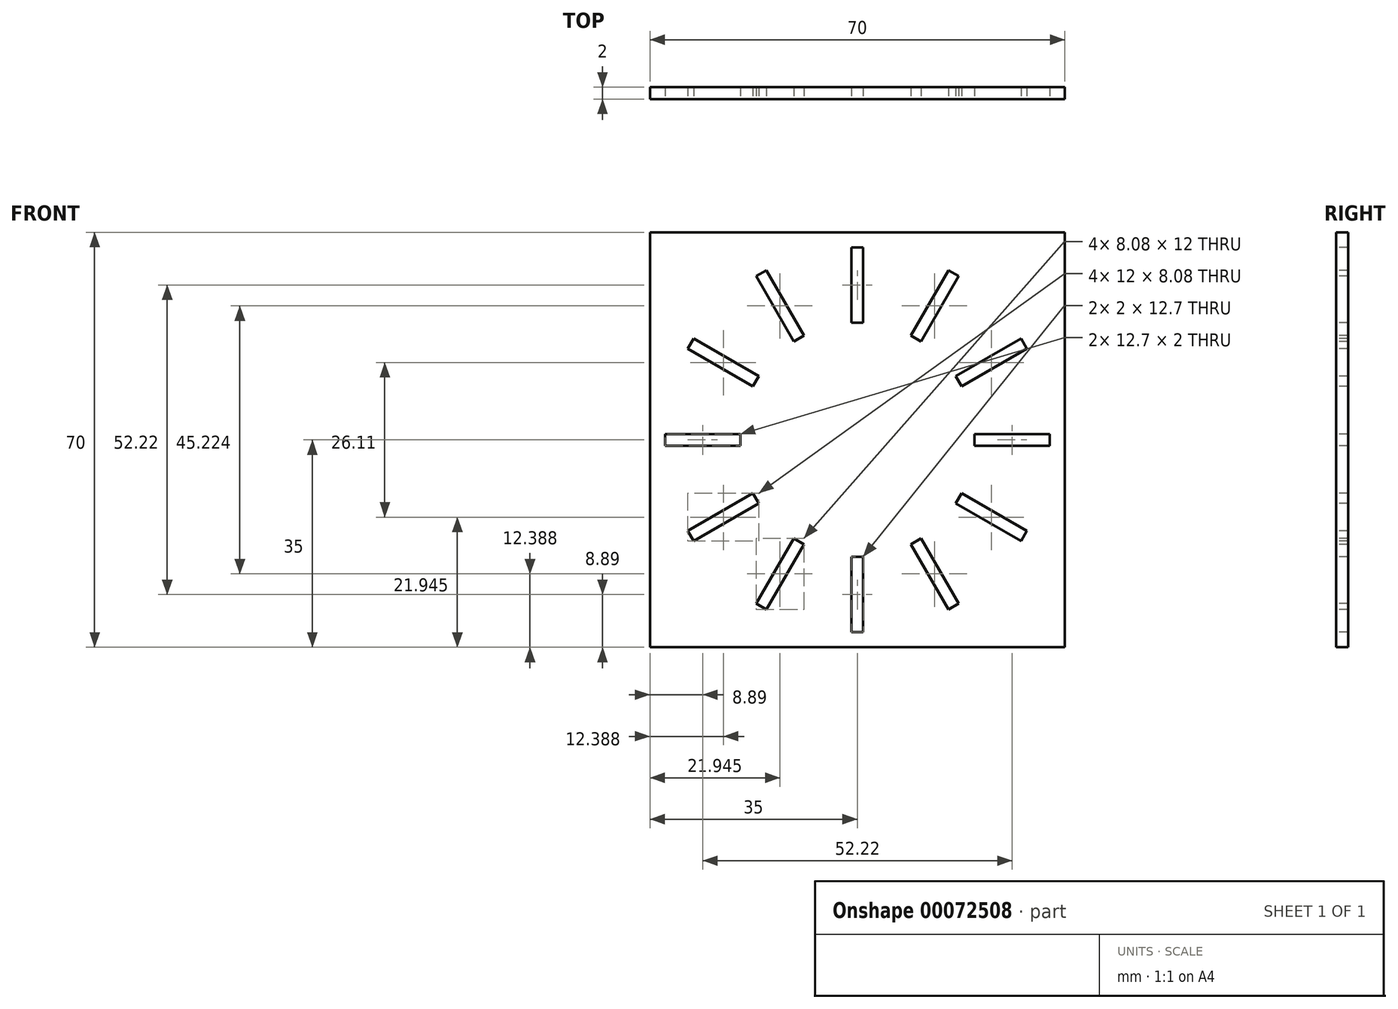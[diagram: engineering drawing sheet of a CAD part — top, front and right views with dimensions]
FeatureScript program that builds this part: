
annotation { "Feature Type Name" : "Feature", "Feature Type Description" : "" }
export const myFeature = defineFeature(function(context is Context, id is Id, definition is map)
    precondition{}
    {
        {
            var Q0;
            Q0=qCreatedBy(makeId("Front.planeOp"),FACE);
            var sketch = newSketch(context, id + "F0", { "sketchPlane" : qUnion([Q0])});
            skLineSegment(sketch, "E0.rect.bottom", {"start": v(-35, 35) * mm, "end": v(35, 35) * mm});
            skLineSegment(sketch, "E0.rect.top", {"start": v(-35, -35) * mm, "end": v(35, -35) * mm});
            skLineSegment(sketch, "E0.rect.left", {"start": v(-35, 35) * mm, "end": v(-35, -35) * mm});
            skLineSegment(sketch, "E0.rect.right", {"start": v(35, 35) * mm, "end": v(35, -35) * mm});
            skPoint(sketch, "E0.rect.middle", {"position": v(0, 0) * mm});
            skSolve(sketch);
        }
        {
            var Q0;
            Q0 = qSketchRegion(id + "F0", true);
            extrude(context, id + "F1", {"entities" : qUnion([Q0]), "endBound" : BoundingType.SYMMETRIC, "depth" : 2 * mm});
        }
        {
            var Q0;
            Q0=makeQuery(id+"F1.opExtrude","CAP_FACE",FACE,{"disambiguationData":[OSD([sQuery(id+"F0.wireOp",EDGE,"E0.rect.bottom"),sQuery(id+"F0.wireOp",EDGE,"E0.rect.top"),sQuery(id+"F0.wireOp",EDGE,"E0.rect.left"),sQuery(id+"F0.wireOp",EDGE,"E0.rect.right")])],"isStart":false});
            var sketch = newSketch(context, id + "F2", { "sketchPlane" : qUnion([Q0])});
            skLineSegment(sketch, "E1.rect.bottom", {"start": v(-1, 32.46) * mm, "end": v(1, 32.46) * mm});
            skLineSegment(sketch, "E1.rect.top", {"start": v(-1, 19.76) * mm, "end": v(1, 19.76) * mm});
            skLineSegment(sketch, "E1.rect.left", {"start": v(-1, 32.46) * mm, "end": v(-1, 19.76) * mm});
            skLineSegment(sketch, "E1.rect.right", {"start": v(1, 32.46) * mm, "end": v(1, 19.76) * mm});
            skPoint(sketch, "E1.rect.middle", {"position": v(0, 26.11) * mm});
            skLineSegment(sketch, "E2.1.0", {"start": v(-15.36, 28.61) * mm, "end": v(-9.01, 17.61) * mm});
            skLineSegment(sketch, "E2.1.1", {"start": v(-17.1, 27.61) * mm, "end": v(-10.75, 16.61) * mm});
            skLineSegment(sketch, "E2.1.2", {"start": v(-10.75, 16.61) * mm, "end": v(-9.01, 17.61) * mm});
            skLineSegment(sketch, "E2.1.3", {"start": v(-17.1, 27.61) * mm, "end": v(-15.36, 28.61) * mm});
            skLineSegment(sketch, "E2.2.0", {"start": v(-27.61, 17.1) * mm, "end": v(-16.61, 10.75) * mm});
            skLineSegment(sketch, "E2.2.1", {"start": v(-28.61, 15.36) * mm, "end": v(-17.61, 9.01) * mm});
            skLineSegment(sketch, "E2.2.2", {"start": v(-17.61, 9.01) * mm, "end": v(-16.61, 10.75) * mm});
            skLineSegment(sketch, "E2.2.3", {"start": v(-28.61, 15.36) * mm, "end": v(-27.61, 17.1) * mm});
            skLineSegment(sketch, "E2.3.0", {"start": v(-32.46, 1) * mm, "end": v(-19.76, 1) * mm});
            skLineSegment(sketch, "E2.3.1", {"start": v(-32.46, -1) * mm, "end": v(-19.76, -1) * mm});
            skLineSegment(sketch, "E2.3.2", {"start": v(-19.76, -1) * mm, "end": v(-19.76, 1) * mm});
            skLineSegment(sketch, "E2.3.3", {"start": v(-32.46, -1) * mm, "end": v(-32.46, 1) * mm});
            skLineSegment(sketch, "E2.4.0", {"start": v(-28.61, -15.36) * mm, "end": v(-17.61, -9.01) * mm});
            skLineSegment(sketch, "E2.4.1", {"start": v(-27.61, -17.1) * mm, "end": v(-16.61, -10.75) * mm});
            skLineSegment(sketch, "E2.4.2", {"start": v(-16.61, -10.75) * mm, "end": v(-17.61, -9.01) * mm});
            skLineSegment(sketch, "E2.4.3", {"start": v(-27.61, -17.1) * mm, "end": v(-28.61, -15.36) * mm});
            skLineSegment(sketch, "E2.5.0", {"start": v(-17.1, -27.61) * mm, "end": v(-10.75, -16.61) * mm});
            skLineSegment(sketch, "E2.5.1", {"start": v(-15.36, -28.61) * mm, "end": v(-9.01, -17.61) * mm});
            skLineSegment(sketch, "E2.5.2", {"start": v(-9.01, -17.61) * mm, "end": v(-10.75, -16.61) * mm});
            skLineSegment(sketch, "E2.5.3", {"start": v(-15.36, -28.61) * mm, "end": v(-17.1, -27.61) * mm});
            skLineSegment(sketch, "E2.6.0", {"start": v(-1, -32.46) * mm, "end": v(-1, -19.76) * mm});
            skLineSegment(sketch, "E2.6.1", {"start": v(1, -32.46) * mm, "end": v(1, -19.76) * mm});
            skLineSegment(sketch, "E2.6.2", {"start": v(1, -19.76) * mm, "end": v(-1, -19.76) * mm});
            skLineSegment(sketch, "E2.6.3", {"start": v(1, -32.46) * mm, "end": v(-1, -32.46) * mm});
            skLineSegment(sketch, "E2.7.0", {"start": v(15.36, -28.61) * mm, "end": v(9.01, -17.61) * mm});
            skLineSegment(sketch, "E2.7.1", {"start": v(17.1, -27.61) * mm, "end": v(10.75, -16.61) * mm});
            skLineSegment(sketch, "E2.7.2", {"start": v(10.75, -16.61) * mm, "end": v(9.01, -17.61) * mm});
            skLineSegment(sketch, "E2.7.3", {"start": v(17.1, -27.61) * mm, "end": v(15.36, -28.61) * mm});
            skLineSegment(sketch, "E2.8.0", {"start": v(27.61, -17.1) * mm, "end": v(16.61, -10.75) * mm});
            skLineSegment(sketch, "E2.8.1", {"start": v(28.61, -15.36) * mm, "end": v(17.61, -9.01) * mm});
            skLineSegment(sketch, "E2.8.2", {"start": v(17.61, -9.01) * mm, "end": v(16.61, -10.75) * mm});
            skLineSegment(sketch, "E2.8.3", {"start": v(28.61, -15.36) * mm, "end": v(27.61, -17.1) * mm});
            skLineSegment(sketch, "E2.9.0", {"start": v(32.46, -1) * mm, "end": v(19.76, -1) * mm});
            skLineSegment(sketch, "E2.9.1", {"start": v(32.46, 1) * mm, "end": v(19.76, 1) * mm});
            skLineSegment(sketch, "E2.9.2", {"start": v(19.76, 1) * mm, "end": v(19.76, -1) * mm});
            skLineSegment(sketch, "E2.9.3", {"start": v(32.46, 1) * mm, "end": v(32.46, -1) * mm});
            skLineSegment(sketch, "E2.10.0", {"start": v(28.61, 15.36) * mm, "end": v(17.61, 9.01) * mm});
            skLineSegment(sketch, "E2.10.1", {"start": v(27.61, 17.1) * mm, "end": v(16.61, 10.75) * mm});
            skLineSegment(sketch, "E2.10.2", {"start": v(16.61, 10.75) * mm, "end": v(17.61, 9.01) * mm});
            skLineSegment(sketch, "E2.10.3", {"start": v(27.61, 17.1) * mm, "end": v(28.61, 15.36) * mm});
            skLineSegment(sketch, "E2.11.0", {"start": v(17.1, 27.61) * mm, "end": v(10.75, 16.61) * mm});
            skLineSegment(sketch, "E2.11.1", {"start": v(15.36, 28.61) * mm, "end": v(9.01, 17.61) * mm});
            skLineSegment(sketch, "E2.11.2", {"start": v(9.01, 17.61) * mm, "end": v(10.75, 16.61) * mm});
            skLineSegment(sketch, "E2.11.3", {"start": v(15.36, 28.61) * mm, "end": v(17.1, 27.61) * mm});
            skPoint(sketch, "E2.center", {"position": v(0, 0) * mm});
            skSolve(sketch);
        }
        {
            var Q0;
            Q0 = qSketchRegion(id + "F2", true);
            extrude(context, id + "F3", {"entities" : qUnion([Q0]), "operationType" : NewBodyOperationType.REMOVE, "endBound" : BoundingType.THROUGH_ALL, "oppositeDirection" : true, "depth" : 25.4 * mm});
        }
    });
